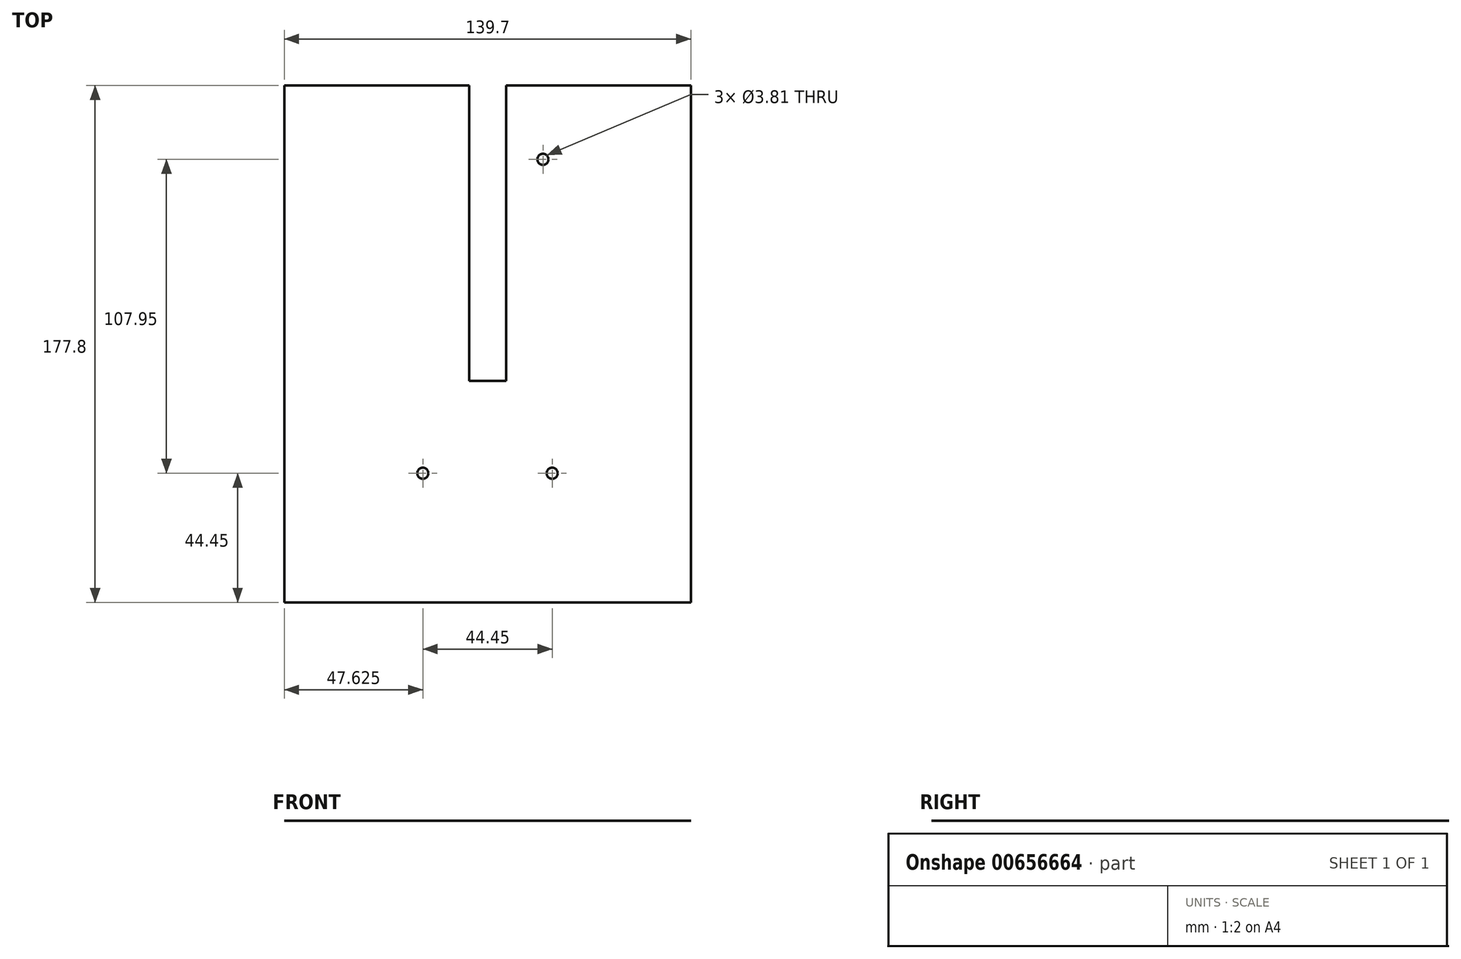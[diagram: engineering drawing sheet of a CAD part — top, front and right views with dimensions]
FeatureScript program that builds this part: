
annotation { "Feature Type Name" : "Feature", "Feature Type Description" : "" }
export const myFeature = defineFeature(function(context is Context, id is Id, definition is map)
    precondition{}
    {
        {
            var Q0;
            Q0=qCreatedBy(makeId("Top.planeOp"),FACE);
            var sketch = newSketch(context, id + "F0", { "sketchPlane" : qUnion([Q0])});
            skLineSegment(sketch, "E0.bottom", {"start": v(0, 177.8) * mm, "end": v(63.5, 177.8) * mm});
            skLineSegment(sketch, "E0.top", {"start": v(0, 0) * mm, "end": v(139.7, 0) * mm});
            skLineSegment(sketch, "E0.left", {"start": v(0, 177.8) * mm, "end": v(0, 0) * mm});
            skLineSegment(sketch, "E0.right", {"start": v(139.7, 177.8) * mm, "end": v(139.7, 0) * mm});
            skLineSegment(sketch, "E1", {"start": v(76.2, 177.8) * mm, "end": v(76.2, 76.2) * mm});
            skLineSegment(sketch, "E2", {"start": v(76.2, 76.2) * mm, "end": v(63.5, 76.2) * mm});
            skLineSegment(sketch, "E3", {"start": v(63.5, 76.2) * mm, "end": v(63.5, 177.8) * mm});
            skLineSegment(sketch, "E4.trimOffspring", {"start": v(76.2, 177.8) * mm, "end": v(139.7, 177.8) * mm});
            skCircle(sketch, "E5", {"center": v(88.9, 152.4) * mm, "radius": 1.9 * mm});
            skCircle(sketch, "E6", {"center": v(47.62, 44.45) * mm, "radius": 1.9 * mm});
            skCircle(sketch, "E7", {"center": v(92.07, 44.45) * mm, "radius": 1.9 * mm});
            skSolve(sketch);
        }
        {
            var Q0;
            Q0 = qSketchRegion(id + "F0", true);
            extrude(context, id + "F1", {"entities" : qUnion([Q0]), "depth" : 1 / 203.2 * mm, "offsetDistance" : 25.4 * mm});
        }
    });
